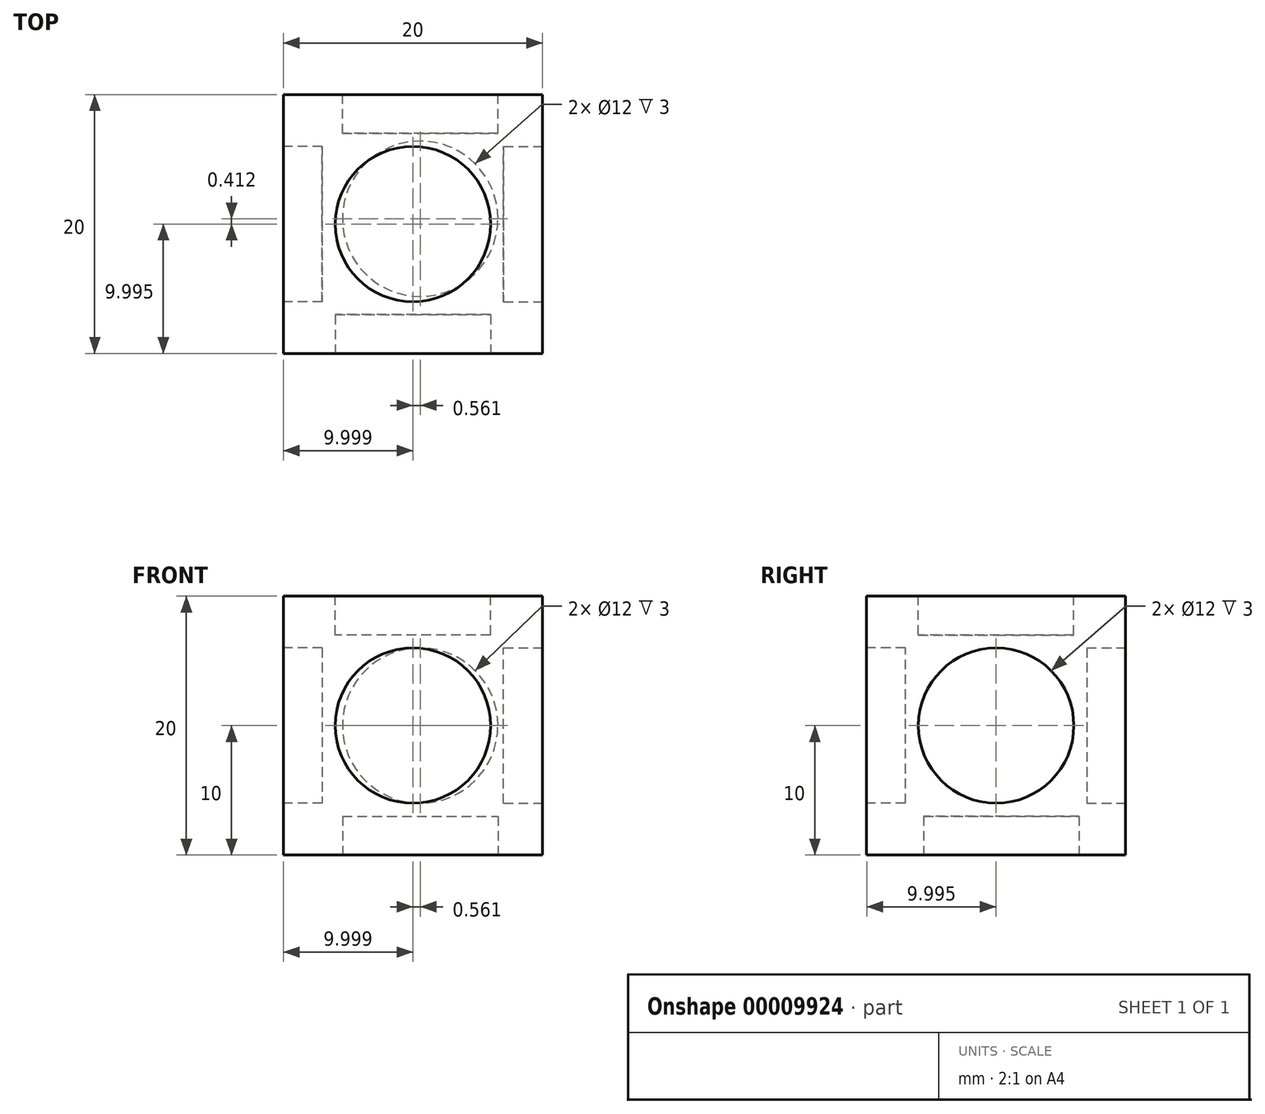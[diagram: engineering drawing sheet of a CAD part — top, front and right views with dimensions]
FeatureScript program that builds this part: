
annotation { "Feature Type Name" : "Feature", "Feature Type Description" : "" }
export const myFeature = defineFeature(function(context is Context, id is Id, definition is map)
    precondition{}
    {
        {
            var Q0;
            Q0=qCreatedBy(makeId("Top.planeOp"),FACE);
            var sketch = newSketch(context, id + "F0", { "sketchPlane" : qUnion([Q0])});
            skLineSegment(sketch, "E0.bottom", {"start": v(-10.56, 8.5) * mm, "end": v(9.44, 8.5) * mm});
            skLineSegment(sketch, "E0.top", {"start": v(-10.56, -11.5) * mm, "end": v(9.44, -11.5) * mm});
            skLineSegment(sketch, "E0.left", {"start": v(-10.56, 8.5) * mm, "end": v(-10.56, -11.5) * mm});
            skLineSegment(sketch, "E0.right", {"start": v(9.44, 8.5) * mm, "end": v(9.44, -11.5) * mm});
            skSolve(sketch);
        }
        {
            var Q0;
            Q0 = qSketchRegion(id + "F0", true);
            extrude(context, id + "F1", {"entities" : qUnion([Q0]), "depth" : 20 * mm});
        }
        {
            var Q0;
            Q0=makeQuery(id+"F1.opExtrude","CAP_FACE",FACE,{"disambiguationData":[OSD([sQuery(id+"F0.wireOp",EDGE,"E0.bottom"),sQuery(id+"F0.wireOp",EDGE,"E0.top"),sQuery(id+"F0.wireOp",EDGE,"E0.left"),sQuery(id+"F0.wireOp",EDGE,"E0.right")])],"isStart":false});
            var sketch = newSketch(context, id + "F2", { "sketchPlane" : qUnion([Q0])});
            skCircle(sketch, "E1", {"center": v(-0.56, -1.5) * mm, "radius": 6 * mm});
            skPoint(sketch, "E1.centerSnap0", {"position": v(9.44, -1.5) * mm});
            skPoint(sketch, "E1.centerSnap1", {"position": v(-0.56, 8.5) * mm});
            skSolve(sketch);
        }
        {
            var Q0;
            Q0 = qSketchRegion(id + "F2", true);
            extrude(context, id + "F3", {"entities" : qUnion([Q0]), "operationType" : NewBodyOperationType.REMOVE, "oppositeDirection" : true, "depth" : 3 * mm});
        }
        {
            var Q0;
            Q0=makeQuery(id+"F1.opExtrude","SWEPT_FACE",FACE,{"disambiguationData":[OSD([sQuery(id+"F0.wireOp",EDGE,"E0.top")])]});
            var sketch = newSketch(context, id + "F4", { "sketchPlane" : qUnion([Q0])});
            skCircle(sketch, "E2", {"center": v(-0.56, 10) * mm, "radius": 6 * mm});
            skPoint(sketch, "E2.centerSnap0", {"position": v(9.44, 10) * mm});
            skPoint(sketch, "E2.centerSnap1", {"position": v(-0.56, 20) * mm});
            skSolve(sketch);
        }
        {
            var Q0;
            Q0 = qSketchRegion(id + "F4", true);
            extrude(context, id + "F5", {"entities" : qUnion([Q0]), "operationType" : NewBodyOperationType.REMOVE, "oppositeDirection" : true, "depth" : 3 * mm});
        }
        {
            var Q0;
            Q0=makeQuery(id+"F1.opExtrude","SWEPT_FACE",FACE,{"disambiguationData":[OSD([sQuery(id+"F0.wireOp",EDGE,"E0.right")])]});
            var sketch = newSketch(context, id + "F6", { "sketchPlane" : qUnion([Q0])});
            skCircle(sketch, "E3", {"center": v(-1.5, 10) * mm, "radius": 6 * mm});
            skPoint(sketch, "E3.centerSnap0", {"position": v(8.5, 10) * mm});
            skPoint(sketch, "E3.centerSnap1", {"position": v(-1.5, 20) * mm});
            skSolve(sketch);
        }
        {
            var Q0;
            Q0 = qSketchRegion(id + "F6", true);
            extrude(context, id + "F7", {"entities" : qUnion([Q0]), "operationType" : NewBodyOperationType.REMOVE, "oppositeDirection" : true, "depth" : 3 * mm});
        }
        {
            var Q0;
            Q0=makeQuery(id+"F1.opExtrude","SWEPT_FACE",FACE,{"disambiguationData":[OSD([sQuery(id+"F0.wireOp",EDGE,"E0.left")])]});
            var sketch = newSketch(context, id + "F8", { "sketchPlane" : qUnion([Q0])});
            skCircle(sketch, "E4", {"center": v(1.5, 10) * mm, "radius": 6 * mm});
            skPoint(sketch, "E4.centerSnap0", {"position": v(11.5, 10) * mm});
            skPoint(sketch, "E4.centerSnap1", {"position": v(1.5, 20) * mm});
            skSolve(sketch);
        }
        {
            var Q0;
            Q0 = qSketchRegion(id + "F8", true);
            extrude(context, id + "F9", {"entities" : qUnion([Q0]), "operationType" : NewBodyOperationType.REMOVE, "oppositeDirection" : true, "depth" : 3 * mm});
        }
        {
            var Q0;
            Q0=makeQuery(id+"F1.opExtrude","SWEPT_FACE",FACE,{"disambiguationData":[OSD([sQuery(id+"F0.wireOp",EDGE,"E0.bottom")])]});
            var sketch = newSketch(context, id + "F10", { "sketchPlane" : qUnion([Q0])});
            skCircle(sketch, "E5", {"center": v(0, 10) * mm, "radius": 6 * mm});
            skPoint(sketch, "E5.centerSnap0", {"position": v(10.56, 10) * mm});
            skSolve(sketch);
        }
        {
            var Q0;
            Q0 = qSketchRegion(id + "F10", true);
            extrude(context, id + "F11", {"entities" : qUnion([Q0]), "operationType" : NewBodyOperationType.REMOVE, "oppositeDirection" : true, "depth" : 3 * mm});
        }
        {
            var Q0;
            Q0=makeQuery(id+"F1.opExtrude","CAP_FACE",FACE,{"disambiguationData":[OSD([sQuery(id+"F0.wireOp",EDGE,"E0.bottom"),sQuery(id+"F0.wireOp",EDGE,"E0.top"),sQuery(id+"F0.wireOp",EDGE,"E0.left"),sQuery(id+"F0.wireOp",EDGE,"E0.right")])],"isStart":true});
            var sketch = newSketch(context, id + "F12", { "sketchPlane" : qUnion([Q0])});
            skCircle(sketch, "E6", {"center": v(0, 1.1) * mm, "radius": 6 * mm});
            skSolve(sketch);
        }
        {
            var Q0;
            Q0 = qSketchRegion(id + "F12", true);
            extrude(context, id + "F13", {"entities" : qUnion([Q0]), "operationType" : NewBodyOperationType.REMOVE, "oppositeDirection" : true, "depth" : 3 * mm});
        }
    });
